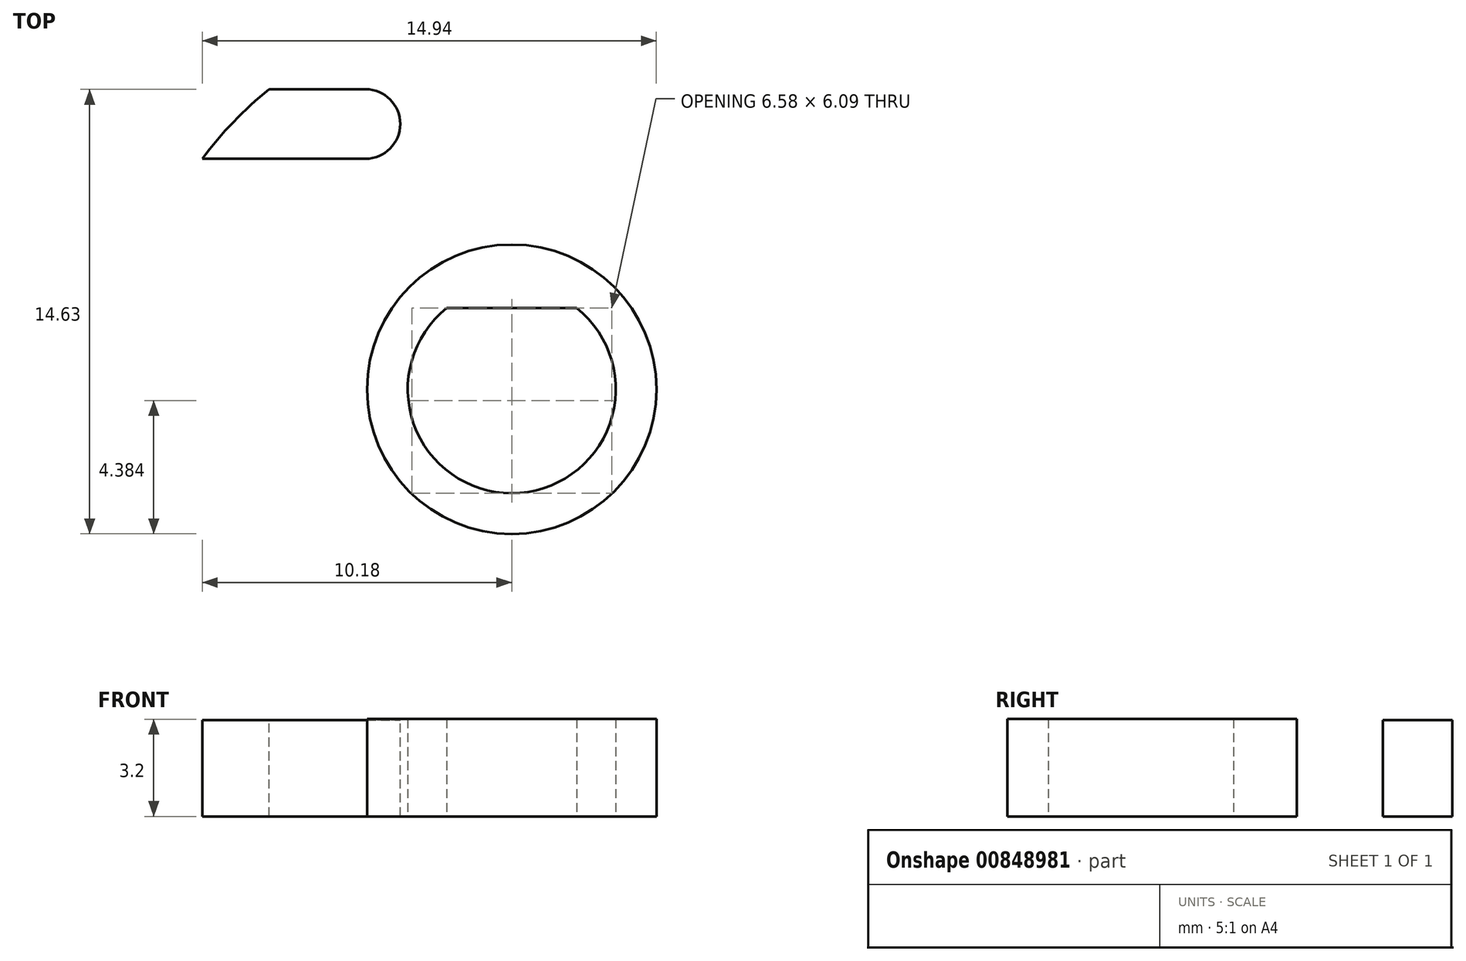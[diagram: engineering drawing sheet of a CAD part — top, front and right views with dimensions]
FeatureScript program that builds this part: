
annotation { "Feature Type Name" : "Feature", "Feature Type Description" : "" }
export const myFeature = defineFeature(function(context is Context, id is Id, definition is map)
    precondition{}
    {
        {
            var Q0;
            Q0=qCreatedBy(makeId("Top.planeOp"),FACE);
            var sketch = newSketch(context, id + "F0", { "sketchPlane" : qUnion([Q0])});
            skArc(sketch, "E0", {"start": v(-2.05, 2.42) * mm, "mid": v(0, -3.17) * mm, "end": v(2.05, 2.42) * mm, "construction": true});
            skLineSegment(sketch, "E1", {"start": v(0, -3.17) * mm, "end": v(0, 2.42) * mm, "construction": true});
            skLineSegment(sketch, "E2", {"start": v(-2.05, 2.42) * mm, "end": v(2.05, 2.42) * mm, "construction": true});
            skArc(sketch, "E3.0", {"start": v(-2.14, 2.67) * mm, "mid": v(0, -3.42) * mm, "end": v(2.14, 2.67) * mm});
            skLineSegment(sketch, "E3.1", {"start": v(-2.14, 2.67) * mm, "end": v(2.14, 2.67) * mm});
            skCircle(sketch, "E4", {"center": v(0, 0) * mm, "radius": 12.7 * mm});
            skSolve(sketch);
        }
        {
            var Q0;
            Q0=makeQuery(id+"F0.imprint","IMPRINT",FACE,{"disambiguationData":[TD([[makeQuery(id+"F0.imprint","IMPRINT",EDGE,{"derivedFrom":sQuery(id+"F0.wireOp",EDGE,"E3.0")}),-1.0]])]});
            extrude(context, id + "F1", {"entities" : qUnion([Q0]), "depth" : 3.17 * mm, "offsetDistance" : 25.4 * mm});
        }
        {
            var Q0;
            Q0=makeQuery(id+"F1.opExtrude","CAP_FACE",FACE,{"disambiguationData":[OSD([sQuery(id+"F0.wireOp",EDGE,"E3.0"),sQuery(id+"F0.wireOp",EDGE,"E3.1"),sQuery(id+"F0.wireOp",EDGE,"E4")])],"isStart":false});
            var sketch = newSketch(context, id + "F2", { "sketchPlane" : qUnion([Q0])});
            skCircle(sketch, "E5", {"center": v(0, 0) * mm, "radius": 4.76 * mm});
            skLineSegment(sketch, "E6", {"start": v(0, 4.76) * mm, "end": v(0, 12.7) * mm, "construction": true});
            skArc(sketch, "E7", {"start": v(-4.81, 9.87) * mm, "mid": v(-3.67, 8.73) * mm, "end": v(-4.81, 7.59) * mm});
            skPoint(sketch, "E7.centerSnap0", {"position": v(0, 8.73) * mm});
            skLineSegment(sketch, "E8", {"start": v(-4.81, 9.87) * mm, "end": v(-7.99, 9.87) * mm});
            skLineSegment(sketch, "E9", {"start": v(-4.81, 7.59) * mm, "end": v(-10.18, 7.59) * mm});
            skSolve(sketch);
        }
        {
            var Q0;
            Q0=makeQuery(id+"F2.imprint","IMPRINT",FACE,{"disambiguationData":[TD([[makeQuery(id+"F2.imprint","IMPRINT",EDGE,{"derivedFrom":sQuery(id+"F2.wireOp",EDGE,"E5")}),1.0]])]});
            extrude(context, id + "F3", {"entities" : qUnion([Q0]), "operationType" : NewBodyOperationType.ADD, "depth" : 11 / 406.4 * mm, "offsetDistance" : 25.4 * mm});
        }
        {
            var Q0;
            Q0=makeQuery(id+"F2.imprint","IMPRINT",FACE,{"disambiguationData":[TD([[makeQuery(id+"F2.imprint","IMPRINT",EDGE,{"derivedFrom":sQuery(id+"F2.wireOp",EDGE,"E7")}),-1.0]])]});
            extrude(context, id + "F4", {"entities" : qUnion([Q0]), "operationType" : NewBodyOperationType.REMOVE, "oppositeDirection" : true, "depth" : 25.4 * mm, "offsetDistance" : 25.4 * mm});
        }
    });
